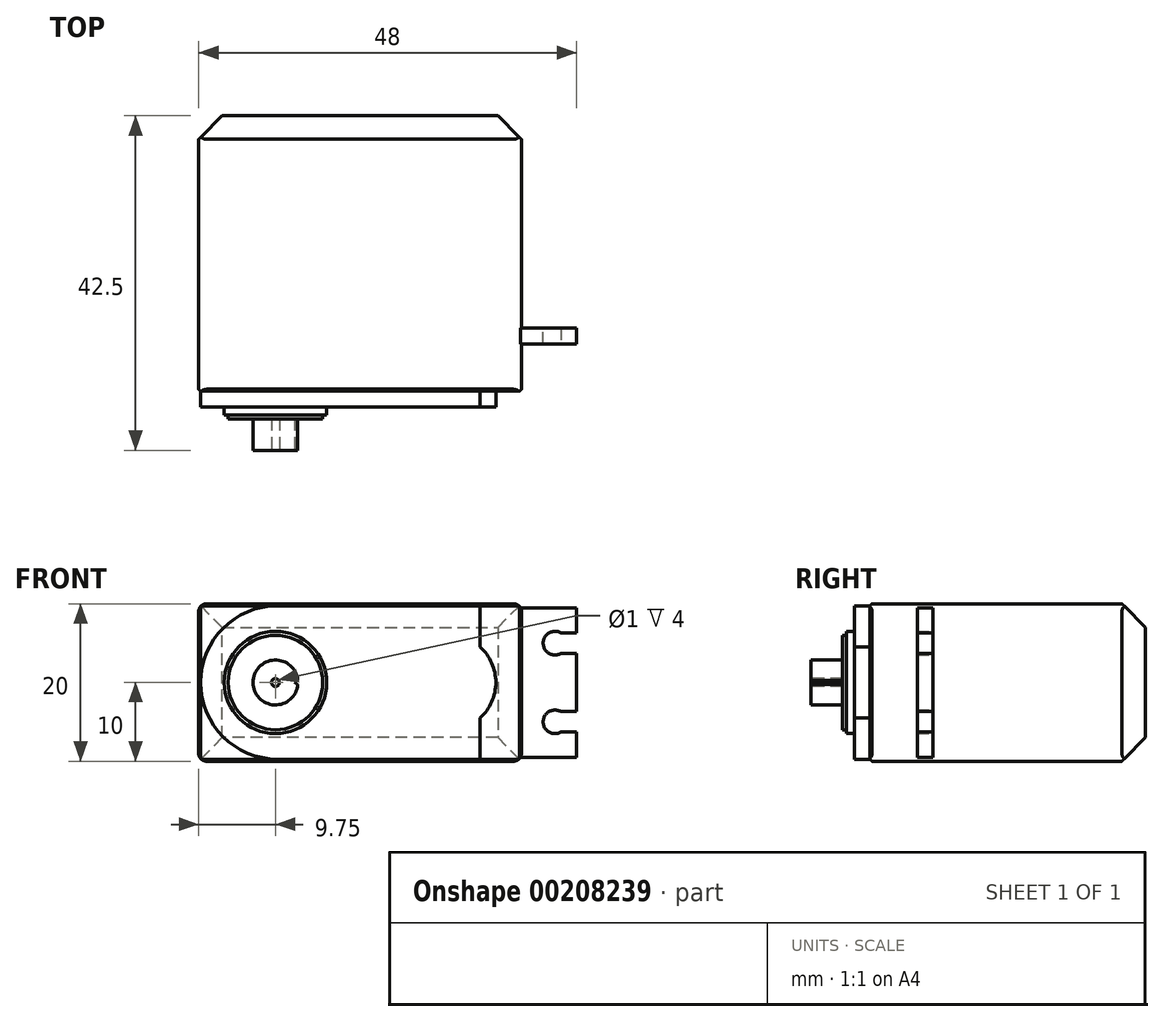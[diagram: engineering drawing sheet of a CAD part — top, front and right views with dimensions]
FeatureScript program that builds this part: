
annotation { "Feature Type Name" : "Feature", "Feature Type Description" : "" }
export const myFeature = defineFeature(function(context is Context, id is Id, definition is map)
    precondition{}
    {
        {
            var Q0;
            Q0=qCreatedBy(makeId("Front.planeOp"),FACE);
            var sketch = newSketch(context, id + "F0", { "sketchPlane" : qUnion([Q0])});
            skLineSegment(sketch, "E0.bottom", {"start": v(-20.5, 10) * mm, "end": v(20.5, 10) * mm});
            skLineSegment(sketch, "E0.top", {"start": v(-20.5, -10) * mm, "end": v(20.5, -10) * mm});
            skLineSegment(sketch, "E0.left", {"start": v(-20.5, 10) * mm, "end": v(-20.5, -10) * mm});
            skLineSegment(sketch, "E0.right", {"start": v(20.5, 10) * mm, "end": v(20.5, -10) * mm});
            skSolve(sketch);
        }
        {
            var Q0;
            Q0=makeQuery(id+"F0.imprint","IMPRINT",FACE,{"disambiguationData":[TD([[makeQuery(id+"F0.imprint","IMPRINT",EDGE,{"derivedFrom":sQuery(id+"F0.wireOp",EDGE,"E0.bottom")}),-1.0]])]});
            extrude(context, id + "F1", {"entities" : qUnion([Q0]), "depth" : 35 * mm});
        }
        {
            var Q0;
            Q0=makeQuery(id+"F1.opExtrude","CAP_EDGE",EDGE,{"disambiguationData":[OSD([sQuery(id+"F0.wireOp",EDGE,"E0.top")])],"isStart":true});
            var Q1;
            Q1=makeQuery(id+"F1.opExtrude","CAP_EDGE",EDGE,{"disambiguationData":[OSD([sQuery(id+"F0.wireOp",EDGE,"E0.right")])],"isStart":true});
            var Q2;
            Q2=makeQuery(id+"F1.opExtrude","CAP_EDGE",EDGE,{"disambiguationData":[OSD([sQuery(id+"F0.wireOp",EDGE,"E0.bottom")])],"isStart":true});
            var Q3;
            Q3=makeQuery(id+"F1.opExtrude","CAP_EDGE",EDGE,{"disambiguationData":[OSD([sQuery(id+"F0.wireOp",EDGE,"E0.left")])],"isStart":true});
            chamfer(context, id + "F2", {"entities" : qUnion([Q0, Q1, Q2, Q3]), "width" : 3 * mm, "tangentPropagation" : true});
        }
        {
            var Q0;
            Q0=makeQuery(id+"F1.opExtrude","CAP_FACE",FACE,{"disambiguationData":[OSD([sQuery(id+"F0.wireOp",EDGE,"E0.bottom"),sQuery(id+"F0.wireOp",EDGE,"E0.top"),sQuery(id+"F0.wireOp",EDGE,"E0.left"),sQuery(id+"F0.wireOp",EDGE,"E0.right")])],"isStart":false});
            chamfer(context, id + "F3", {"entities" : qUnion([Q0]), "width" : .25 * mm, "tangentPropagation" : true});
        }
        {
            var Q0;
            Q0=makeQuery(id+"F1.opExtrude","CAP_FACE",FACE,{"disambiguationData":[OSD([sQuery(id+"F0.wireOp",EDGE,"E0.bottom"),sQuery(id+"F0.wireOp",EDGE,"E0.top"),sQuery(id+"F0.wireOp",EDGE,"E0.left"),sQuery(id+"F0.wireOp",EDGE,"E0.right")])],"isStart":false});
            var sketch = newSketch(context, id + "F4", { "sketchPlane" : qUnion([Q0])});
            skArc(sketch, "E1", {"start": v(-10.5, 9.75) * mm, "mid": v(-20.25, 0) * mm, "end": v(-10.5, -9.75) * mm});
            skPoint(sketch, "E2.0.end.orphan", {"position": v(-20.25, -9.75) * mm});
            skPoint(sketch, "E2.0.start.orphan", {"position": v(-20.25, 9.75) * mm});
            skLineSegment(sketch, "E3.0", {"start": v(15.25, 9.75) * mm, "end": v(-10.5, 9.75) * mm});
            skLineSegment(sketch, "E4.0", {"start": v(-10.5, -9.75) * mm, "end": v(15.25, -9.75) * mm});
            skPoint(sketch, "E5.0.end.orphan", {"position": v(-20.5, 10) * mm});
            skPoint(sketch, "E5.0.start.orphan", {"position": v(-20.5, -10) * mm});
            skLineSegment(sketch, "E6.0", {"start": v(-20.25, 9.75) * mm, "end": v(-20.25, -9.75) * mm});
            skLineSegment(sketch, "E7", {"start": v(15.25, 9.75) * mm, "end": v(15.25, 4.5) * mm});
            skPoint(sketch, "E8.orphan", {"position": v(20.25, 9.75) * mm});
            skPoint(sketch, "E9.orphan", {"position": v(20.25, -9.75) * mm});
            skArc(sketch, "E10", {"start": v(15.25, -4.5) * mm, "mid": v(17.25, 0) * mm, "end": v(15.25, 4.5) * mm});
            skPoint(sketch, "E11", {"position": v(15.25, 4.5) * mm});
            skPoint(sketch, "E12", {"position": v(15.25, -4.5) * mm});
            skLineSegment(sketch, "E13.trimOffspring", {"start": v(15.25, -4.5) * mm, "end": v(15.25, -9.75) * mm});
            skSolve(sketch);
        }
        {
            var Q0;
            {var subQ1=sQuery(id+"F4.wireOp",EDGE,"E3.0");Q0=makeQuery(id+"F4.imprint","IMPRINT",FACE,{"disambiguationData":[TD([[makeQuery(id+"F4.imprint","IMPRINT",EDGE,{"derivedFrom":subQ1}),1.0]])]});}
            extrude(context, id + "F5", {"entities" : qUnion([Q0]), "operationType" : NewBodyOperationType.ADD, "depth" : 2 * mm});
        }
        {
            var Q0;
            Q0=makeQuery(id+"F5.opExtrude","CAP_FACE",FACE,{"disambiguationData":[OSD([sQuery(id+"F4.wireOp",EDGE,"E1"),sQuery(id+"F4.wireOp",EDGE,"E3.0"),sQuery(id+"F4.wireOp",EDGE,"E4.0"),sQuery(id+"F4.wireOp",EDGE,"E7"),sQuery(id+"F4.wireOp",EDGE,"E10"),sQuery(id+"F4.wireOp",EDGE,"E13.trimOffspring")])],"isStart":false});
            var sketch = newSketch(context, id + "F6", { "sketchPlane" : qUnion([Q0])});
            skCircle(sketch, "E14", {"center": v(-10.75, 0) * mm, "radius": 6.5 * mm});
            skSolve(sketch);
        }
        {
            var Q0;
            Q0=makeQuery(id+"F6.imprint","IMPRINT",FACE,{"disambiguationData":[TD([[makeQuery(id+"F6.imprint","IMPRINT",EDGE,{"derivedFrom":sQuery(id+"F6.wireOp",EDGE,"E14")}),1.0]])]});
            extrude(context, id + "F7", {"entities" : qUnion([Q0]), "operationType" : NewBodyOperationType.ADD, "depth" : 1 * mm});
        }
        {
            var Q0;
            Q0=makeQuery(id+"F7.opExtrude","CAP_FACE",FACE,{"disambiguationData":[OSD([sQuery(id+"F6.wireOp",EDGE,"E14")])],"isStart":false});
            var sketch = newSketch(context, id + "F8", { "sketchPlane" : qUnion([Q0])});
            skCircle(sketch, "E15", {"center": v(-10.75, 0) * mm, "radius": 6 * mm});
            skSolve(sketch);
        }
        {
            var Q0;
            Q0=makeQuery(id+"F8.imprint","IMPRINT",FACE,{"disambiguationData":[TD([[makeQuery(id+"F8.imprint","IMPRINT",EDGE,{"derivedFrom":sQuery(id+"F8.wireOp",EDGE,"E15")}),1.0]])]});
            extrude(context, id + "F9", {"entities" : qUnion([Q0]), "operationType" : NewBodyOperationType.ADD, "depth" : .5 * mm});
        }
        {
            var Q0;
            {var subQ0=sQuery(id+"F0.wireOp",EDGE,"E0.right");var subQ1=sQuery(id+"F0.wireOp",EDGE,"E0.top");var subQ2=sQuery(id+"F0.wireOp",EDGE,"E0.bottom");Q0=makeQuery(id+"F5.boolean.opBoolean","SPLIT",FACE,{"disambiguationData":[TD([makeQuery(id+"F3.opChamfer","BLEND_FACE",FACE,{"disambiguationData":[OSD([subQ2])]}),makeQuery(id+"F3.opChamfer","BLEND_FACE",FACE,{"disambiguationData":[OSD([subQ1])]}),makeQuery(id+"F3.opChamfer","BLEND_FACE",FACE,{"disambiguationData":[OSD([subQ0])]}),makeQuery(id+"F5.opExtrude","SWEPT_FACE",FACE,{"disambiguationData":[OSD([sQuery(id+"F4.wireOp",EDGE,"E3.0")])]}),makeQuery(id+"F5.opExtrude","SWEPT_FACE",FACE,{"disambiguationData":[OSD([sQuery(id+"F4.wireOp",EDGE,"E4.0")])]}),makeQuery(id+"F5.opExtrude","SWEPT_FACE",FACE,{"disambiguationData":[OSD([sQuery(id+"F4.wireOp",EDGE,"E7")])]}),makeQuery(id+"F5.opExtrude","SWEPT_FACE",FACE,{"disambiguationData":[OSD([sQuery(id+"F4.wireOp",EDGE,"E10")])]}),makeQuery(id+"F5.opExtrude","SWEPT_FACE",FACE,{"disambiguationData":[OSD([sQuery(id+"F4.wireOp",EDGE,"E13.trimOffspring")])]})])],"derivedFrom":makeQuery(id+"F1.opExtrude","CAP_FACE",FACE,{"disambiguationData":[OSD([subQ2,subQ1,sQuery(id+"F0.wireOp",EDGE,"E0.left"),subQ0])],"isStart":false})});}
            cPlane(context, id + "F10", {"entities" : qUnion([Q0]), "cplaneType" : CPlaneType.OFFSET, "offset" : 8 * mm, "oppositeDirection" : true, "width" : 150 * mm, "height" : 150 * mm});
        }
        {
            var Q0;
            Q0=qCreatedBy(id+"F10.planeOp",FACE);
            var sketch = newSketch(context, id + "F11", { "sketchPlane" : qUnion([Q0])});
            skLineSegment(sketch, "E16.0", {"start": v(20.5, 9.5) * mm, "end": v(20.5, -9.5) * mm});
            skLineSegment(sketch, "E17.right", {"start": v(27.5, 9.5) * mm, "end": v(27.5, -9.5) * mm});
            skLineSegment(sketch, "E18.0", {"start": v(-20.5, -9.5) * mm, "end": v(-20.5, 9.5) * mm});
            skLineSegment(sketch, "E19.left", {"start": v(-20.5, 9.5) * mm, "end": v(-20.5, -9.5) * mm});
            skLineSegment(sketch, "E19.right", {"start": v(-27.5, 9.5) * mm, "end": v(-27.5, -9.5) * mm});
            skCircle(sketch, "E20", {"center": v(-24.75, 5) * mm, "radius": 1.5 * mm});
            skCircle(sketch, "E21", {"center": v(-24.75, -5) * mm, "radius": 1.5 * mm});
            skCircle(sketch, "E22", {"center": v(24.75, 5) * mm, "radius": 1.5 * mm});
            skCircle(sketch, "E23", {"center": v(24.75, -5) * mm, "radius": 1.5 * mm});
            skLineSegment(sketch, "E24", {"start": v(-27.5, -9.5) * mm, "end": v(-20.5, -9.5) * mm});
            skLineSegment(sketch, "E25", {"start": v(-27.5, 9.5) * mm, "end": v(-20.5, 9.5) * mm});
            skLineSegment(sketch, "E26", {"start": v(27.5, 9.5) * mm, "end": v(20.5, 9.5) * mm});
            skLineSegment(sketch, "E27", {"start": v(27.5, -9.5) * mm, "end": v(20.5, -9.5) * mm});
            skSolve(sketch);
        }
        {
            var Q0;
            Q0=makeQuery(id+"F11.imprint","IMPRINT",FACE,{"disambiguationData":[TD([[makeQuery(id+"F11.imprint","IMPRINT",EDGE,{"derivedFrom":sQuery(id+"F11.wireOp",EDGE,"E19.left")}),-1.0]])]});
            var Q1;
            Q1=makeQuery(id+"F11.imprint","IMPRINT",FACE,{"disambiguationData":[TD([[makeQuery(id+"F11.imprint","IMPRINT",EDGE,{"derivedFrom":sQuery(id+"F11.wireOp",EDGE,"E16.0")}),1.0]])]});
            extrude(context, id + "F12", {"entities" : qUnion([Q0, Q1]), "operationType" : NewBodyOperationType.ADD, "depth" : 2 * mm});
        }
        {
            var Q0;
            Q0=makeQuery(id+"F9.opExtrude","CAP_FACE",FACE,{"disambiguationData":[OSD([sQuery(id+"F8.wireOp",EDGE,"E15")])],"isStart":false});
            var sketch = newSketch(context, id + "F13", { "sketchPlane" : qUnion([Q0])});
            skCircle(sketch, "E28", {"center": v(-10.75, 0) * mm, "radius": 2.85 * mm});
            skSolve(sketch);
        }
        {
            var Q0;
            Q0 = qSketchRegion(id + "F13", true);
            var Q1;
            Q1=makeQuery(id+"FYYqpiqxGiRtzgj_1.opExtrude","CAP_FACE",FACE,{"disambiguationData":[OSD([sQuery(id+"F13.wireOp",EDGE,"E28")])],"isStart":false});
            extrude(context, id + "F14", {"entities" : qUnion([Q0, Q1]), "operationType" : NewBodyOperationType.ADD, "depth" : 4 * mm});
        }
        {
            var Q0;
            Q0=makeQuery(id+"F12.opExtrude","CAP_FACE",FACE,{"disambiguationData":[OSD([sQuery(id+"F11.wireOp",EDGE,"E16.0"),sQuery(id+"F11.wireOp",EDGE,"E17.right"),sQuery(id+"F11.wireOp",EDGE,"E22"),sQuery(id+"F11.wireOp",EDGE,"E23"),sQuery(id+"F11.wireOp",EDGE,"E26"),sQuery(id+"F11.wireOp",EDGE,"E27")])],"isStart":false});
            var sketch = newSketch(context, id + "F15", { "sketchPlane" : qUnion([Q0])});
            skLineSegment(sketch, "E29", {"start": v(27.5, 6.3) * mm, "end": v(25.5, 6.3) * mm});
            skLineSegment(sketch, "E30", {"start": v(27.5, 3.7) * mm, "end": v(25.5, 3.7) * mm});
            skLineSegment(sketch, "E31", {"start": v(27.5, -3.7) * mm, "end": v(25.5, -3.7) * mm});
            skLineSegment(sketch, "E32", {"start": v(27.5, -6.3) * mm, "end": v(25.5, -6.3) * mm});
            skArc(sketch, "E33.0", {"start": v(25.5, 6.3) * mm, "mid": v(23.25, 5) * mm, "end": v(25.5, 3.7) * mm});
            skArc(sketch, "E34.0", {"start": v(25.5, -3.7) * mm, "mid": v(23.25, -5) * mm, "end": v(25.5, -6.3) * mm});
            skCircle(sketch, "E35.0", {"center": v(-24.75, 5) * mm, "radius": 1.5 * mm});
            skCircle(sketch, "E36.0", {"center": v(-24.75, -5) * mm, "radius": 1.5 * mm});
            skLineSegment(sketch, "E37.0", {"start": v(-27.5, 6.3) * mm, "end": v(-27.5, 3.7) * mm});
            skLineSegment(sketch, "E38", {"start": v(-25.5, 3.7) * mm, "end": v(-27.5, 3.7) * mm});
            skLineSegment(sketch, "E39", {"start": v(-25.5, -6.3) * mm, "end": v(-27.5, -6.3) * mm});
            skLineSegment(sketch, "E40", {"start": v(-25.5, -3.7) * mm, "end": v(-27.5, -3.7) * mm});
            skLineSegment(sketch, "E41", {"start": v(-25.5, 6.3) * mm, "end": v(-27.5, 6.3) * mm});
            skLineSegment(sketch, "E42.0", {"start": v(27.5, 6.3) * mm, "end": v(27.5, 3.7) * mm});
            skPoint(sketch, "E43.orphan", {"position": v(27.5, 9.5) * mm});
            skLineSegment(sketch, "E44.trimOffspring", {"start": v(27.5, -3.7) * mm, "end": v(27.5, -6.3) * mm});
            skPoint(sketch, "E45.orphan", {"position": v(27.5, -9.5) * mm});
            skPoint(sketch, "E46.trimOffspring.end.orphan", {"position": v(-27.5, -9.5) * mm});
            skPoint(sketch, "E47.orphan", {"position": v(-27.5, 9.5) * mm});
            skLineSegment(sketch, "E48.0.0", {"start": v(-20.5, -9.5) * mm, "end": v(-20.5, 9.5) * mm});
            skLineSegment(sketch, "E48.0.1", {"start": v(-20.5, 9.5) * mm, "end": v(-27.5, 9.5) * mm});
            skLineSegment(sketch, "E48.0.3", {"start": v(-27.5, -9.5) * mm, "end": v(-20.5, -9.5) * mm});
            skLineSegment(sketch, "E49.trimOffspring", {"start": v(-27.5, -3.7) * mm, "end": v(-27.5, -6.3) * mm});
            skSolve(sketch);
        }
        {
            var Q0;
            {var subQ0=sQuery(id+"F15.wireOp",EDGE,"E38");Q0=makeQuery(id+"F15.imprint","IMPRINT",FACE,{"disambiguationData":[TD([[makeQuery(id+"F15.imprint","IMPRINT",EDGE,{"derivedFrom":subQ0}),-1.0]])]});}
            var Q1;
            {var subQ0=sQuery(id+"F15.wireOp",EDGE,"E39");Q1=makeQuery(id+"F15.imprint","IMPRINT",FACE,{"disambiguationData":[TD([[makeQuery(id+"F15.imprint","IMPRINT",EDGE,{"derivedFrom":subQ0}),-1.0]])]});}
            var Q2;
            {var subQ0=sQuery(id+"F15.wireOp",EDGE,"E29");Q2=makeQuery(id+"F15.imprint","IMPRINT",FACE,{"disambiguationData":[TD([[makeQuery(id+"F15.imprint","IMPRINT",EDGE,{"derivedFrom":subQ0}),1.0]])]});}
            var Q3;
            {var subQ0=sQuery(id+"F15.wireOp",EDGE,"E31");Q3=makeQuery(id+"F15.imprint","IMPRINT",FACE,{"disambiguationData":[TD([[makeQuery(id+"F15.imprint","IMPRINT",EDGE,{"derivedFrom":subQ0}),1.0]])]});}
            extrude(context, id + "F16", {"entities" : qUnion([Q0, Q1, Q2, Q3]), "operationType" : NewBodyOperationType.REMOVE, "oppositeDirection" : true, "depth" : 25 * mm});
        }
        {
            var Q0;
            Q0=makeQuery(id+"F14.opExtrude","CAP_FACE",FACE,{"disambiguationData":[OSD([sQuery(id+"F13.wireOp",EDGE,"E28")])],"isStart":false});
            var sketch = newSketch(context, id + "F17", { "sketchPlane" : qUnion([Q0])});
            skArc(sketch, "E50.0", {"start": v(-7.91, -0.25) * mm, "mid": v(-7.9, 0) * mm, "end": v(-7.91, 0.25) * mm});
            skLineSegment(sketch, "E51", {"start": v(-10.75, 0) * mm, "end": v(-6.1, 0) * mm, "construction": true});
            skLineSegment(sketch, "E52", {"start": v(-7.91, 0.25) * mm, "end": v(-8.34, 0) * mm});
            skLineSegment(sketch, "E53.MirrorCS", {"start": v(-7.91, -0.25) * mm, "end": v(-8.34, 0) * mm});
            skSolve(sketch);
        }
        {
            var Q0;
            Q0=makeQuery(id+"F17.imprint","IMPRINT",FACE,{"disambiguationData":[TD([[makeQuery(id+"F17.imprint","IMPRINT",EDGE,{"derivedFrom":sQuery(id+"F17.wireOp",EDGE,"E50.0")}),1.0]])]});
            extrude(context, id + "F18", {"entities" : qUnion([Q0]), "operationType" : NewBodyOperationType.REMOVE, "oppositeDirection" : true, "depth" : 4 * mm});
        }
        {
            var Q0;
            Q0=makeQuery(id+"F14.opExtrude","CAP_FACE",FACE,{"disambiguationData":[OSD([sQuery(id+"F13.wireOp",EDGE,"E28")])],"isStart":false});
            var sketch = newSketch(context, id + "F19", { "sketchPlane" : qUnion([Q0])});
            skCircle(sketch, "E54", {"center": v(-10.75, 0) * mm, "radius": 0.5 * mm});
            skSolve(sketch);
        }
        {
            var Q0;
            Q0=makeQuery(id+"F19.imprint","IMPRINT",FACE,{"disambiguationData":[TD([[makeQuery(id+"F19.imprint","IMPRINT",EDGE,{"derivedFrom":sQuery(id+"F19.wireOp",EDGE,"E54")}),1.0]])]});
            extrude(context, id + "F20", {"entities" : qUnion([Q0]), "operationType" : NewBodyOperationType.REMOVE, "oppositeDirection" : true, "depth" : 4 * mm});
        }
        {
            var Q0;
            Q0=makeQuery(id+"F1.opExtrude","SWEPT_EDGE",EDGE,{"disambiguationData":[OSD([sQuery(id+"F0.wireOp",EDGE,"E0.top"),sQuery(id+"F0.wireOp",EDGE,"E0.left")])]});
            var Q1;
            Q1=makeQuery(id+"F1.opExtrude","SWEPT_EDGE",EDGE,{"disambiguationData":[OSD([sQuery(id+"F0.wireOp",EDGE,"E0.top"),sQuery(id+"F0.wireOp",EDGE,"E0.right")])]});
            var Q2;
            Q2=makeQuery(id+"F1.opExtrude","SWEPT_EDGE",EDGE,{"disambiguationData":[OSD([sQuery(id+"F0.wireOp",EDGE,"E0.bottom"),sQuery(id+"F0.wireOp",EDGE,"E0.right")])]});
            var Q3;
            Q3=makeQuery(id+"F1.opExtrude","SWEPT_EDGE",EDGE,{"disambiguationData":[OSD([sQuery(id+"F0.wireOp",EDGE,"E0.bottom"),sQuery(id+"F0.wireOp",EDGE,"E0.left")])]});
            fillet(context, id + "F21", {"entities" : qUnion([Q0, Q1, Q2, Q3]), "radius" : 1 * mm, "tangentPropagation" : true, "allowEdgeOverflow" : false});
        }
    });
